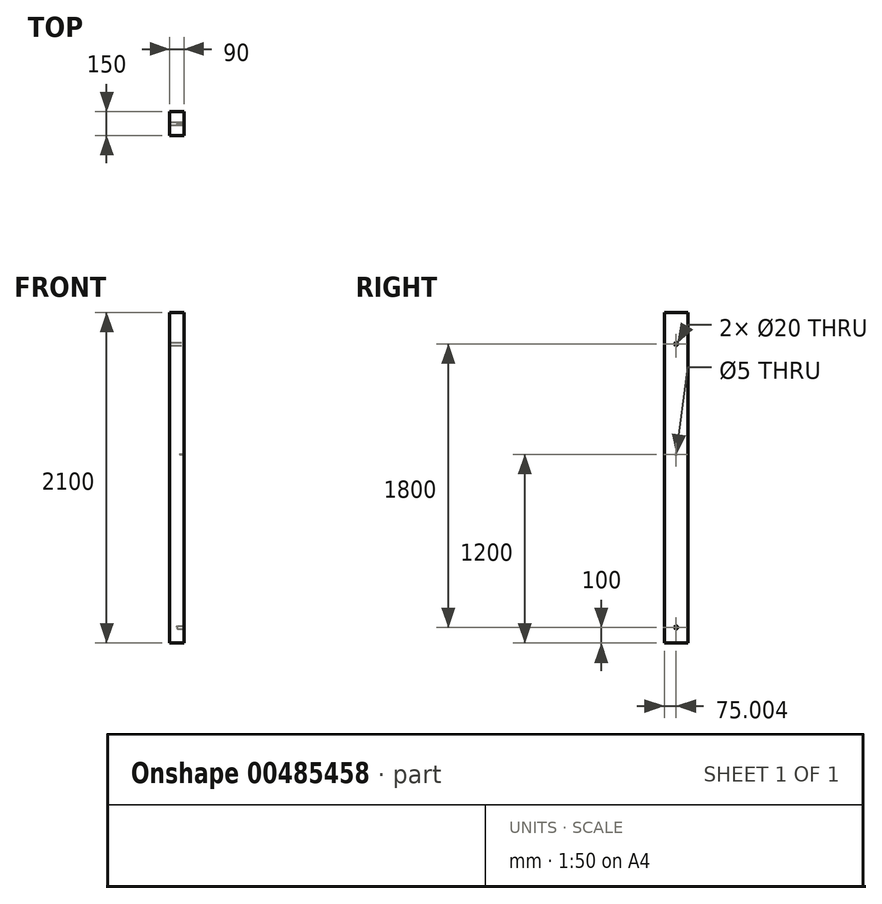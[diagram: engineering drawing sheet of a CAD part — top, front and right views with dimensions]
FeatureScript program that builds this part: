
annotation { "Feature Type Name" : "Feature", "Feature Type Description" : "" }
export const myFeature = defineFeature(function(context is Context, id is Id, definition is map)
    precondition{}
    {
        {
            var Q0;
            Q0=qCreatedBy(makeId("Top.planeOp"),FACE);
            var sketch = newSketch(context, id + "F0", { "sketchPlane" : qUnion([Q0])});
            skLineSegment(sketch, "E0.bottom", {"start": v(-45, 141.65) * mm, "end": v(45, 141.65) * mm});
            skLineSegment(sketch, "E0.top", {"start": v(-45, -8.35) * mm, "end": v(45, -8.35) * mm});
            skLineSegment(sketch, "E0.left", {"start": v(-45, 141.65) * mm, "end": v(-45, -8.35) * mm});
            skLineSegment(sketch, "E0.right", {"start": v(45, 141.65) * mm, "end": v(45, -8.35) * mm});
            skPoint(sketch, "E0.middle", {"position": v(0, 66.65) * mm});
            skLineSegment(sketch, "E1.bottom", {"start": v(34.26, 141.65) * mm, "end": v(-34.26, 141.65) * mm});
            skLineSegment(sketch, "E1.top", {"start": v(34.26, 141.65) * mm, "end": v(-34.26, 141.65) * mm});
            skLineSegment(sketch, "E1.left", {"start": v(34.26, 141.65) * mm, "end": v(34.26, 141.65) * mm});
            skLineSegment(sketch, "E1.right", {"start": v(-34.26, 141.65) * mm, "end": v(-34.26, 141.65) * mm});
            skPoint(sketch, "E1.middle", {"position": v(0, 141.65) * mm});
            skSolve(sketch);
        }
        {
            var Q0;
            Q0=makeQuery(id+"F0.imprint","IMPRINT",FACE,{"disambiguationData":[TD([[makeQuery(id+"F0.imprint","IMPRINT",EDGE,{"derivedFrom":sQuery(id+"F0.wireOp",EDGE,"E0.top")}),1.0]])]});
            extrude(context, id + "F1", {"entities" : qUnion([Q0]), "depth" : 2100 * mm});
        }
        {
            var Q0;
            Q0=makeQuery(id+"F1.opExtrude","SWEPT_FACE",FACE,{"disambiguationData":[OSD([sQuery(id+"F0.wireOp",EDGE,"E0.right")])]});
            var sketch = newSketch(context, id + "F2", { "sketchPlane" : qUnion([Q0])});
            skCircle(sketch, "E2", {"center": v(66.65, 1900) * mm, "radius": 10 * mm});
            skSolve(sketch);
        }
        {
            var Q0;
            Q0=sQuery(id+"F2.wireOp",VERTEX,"E2.center");
            var Q1;
            Q1=makeQuery(id+"F1.opExtrude","SWEPT_BODY",BODY,{"disambiguationData":[OSD([sQuery(id+"F0.wireOp",EDGE,"E0.bottom"),sQuery(id+"F0.wireOp",EDGE,"E0.top"),sQuery(id+"F0.wireOp",EDGE,"E0.left"),sQuery(id+"F0.wireOp",EDGE,"E0.right"),sQuery(id+"F0.wireOp",EDGE,"E1.top")])]});
            hole(context, id + "F3", {"style" : HoleStyle.SIMPLE, "endStyle" : HoleEndStyle.THROUGH, "holeDiameter" : 20 * mm, "isTappedThrough" : true, "tappedDepth" : 12 * mm, "tapClearance" : 3, "locations" : qUnion([Q0]), "scope" : qUnion([Q1])});
        }
        {
            var Q0;
            Q0=makeQuery(id+"F1.opExtrude","SWEPT_FACE",FACE,{"disambiguationData":[OSD([sQuery(id+"F0.wireOp",EDGE,"E0.right")])]});
            var sketch = newSketch(context, id + "F4", { "sketchPlane" : qUnion([Q0])});
            skPoint(sketch, "E3", {"position": v(66.65, 100) * mm});
            skPoint(sketch, "E4", {"position": v(66.65, 1200) * mm});
            skSolve(sketch);
        }
        {
            var Q0;
            Q0=sQuery(id+"F4.wireOp",VERTEX,"E3");
            var Q1;
            Q1=makeQuery(id+"F1.opExtrude","SWEPT_BODY",BODY,{"disambiguationData":[OSD([sQuery(id+"F0.wireOp",EDGE,"E0.bottom"),sQuery(id+"F0.wireOp",EDGE,"E0.top"),sQuery(id+"F0.wireOp",EDGE,"E0.left"),sQuery(id+"F0.wireOp",EDGE,"E0.right"),sQuery(id+"F0.wireOp",EDGE,"E1.top")])]});
            hole(context, id + "F5", {"style" : HoleStyle.SIMPLE, "endStyle" : HoleEndStyle.BLIND, "holeDiameter" : 20 * mm, "holeDepth" : 40 * mm, "isTappedThrough" : true, "tappedDepth" : 12 * mm, "tapClearance" : 3, "locations" : qUnion([Q0]), "scope" : qUnion([Q1])});
        }
        {
            var Q0;
            Q0=sQuery(id+"F4.wireOp",VERTEX,"E4");
            var Q1;
            Q1=makeQuery(id+"F1.opExtrude","SWEPT_BODY",BODY,{"disambiguationData":[OSD([sQuery(id+"F0.wireOp",EDGE,"E0.bottom"),sQuery(id+"F0.wireOp",EDGE,"E0.top"),sQuery(id+"F0.wireOp",EDGE,"E0.left"),sQuery(id+"F0.wireOp",EDGE,"E0.right"),sQuery(id+"F0.wireOp",EDGE,"E1.top")])]});
            hole(context, id + "F6", {"style" : HoleStyle.SIMPLE, "endStyle" : HoleEndStyle.BLIND, "holeDiameter" : 5 * mm, "holeDepth" : 25 * mm, "isTappedThrough" : true, "tappedDepth" : 12 * mm, "tapClearance" : 3, "locations" : qUnion([Q0]), "scope" : qUnion([Q1])});
        }
    });
